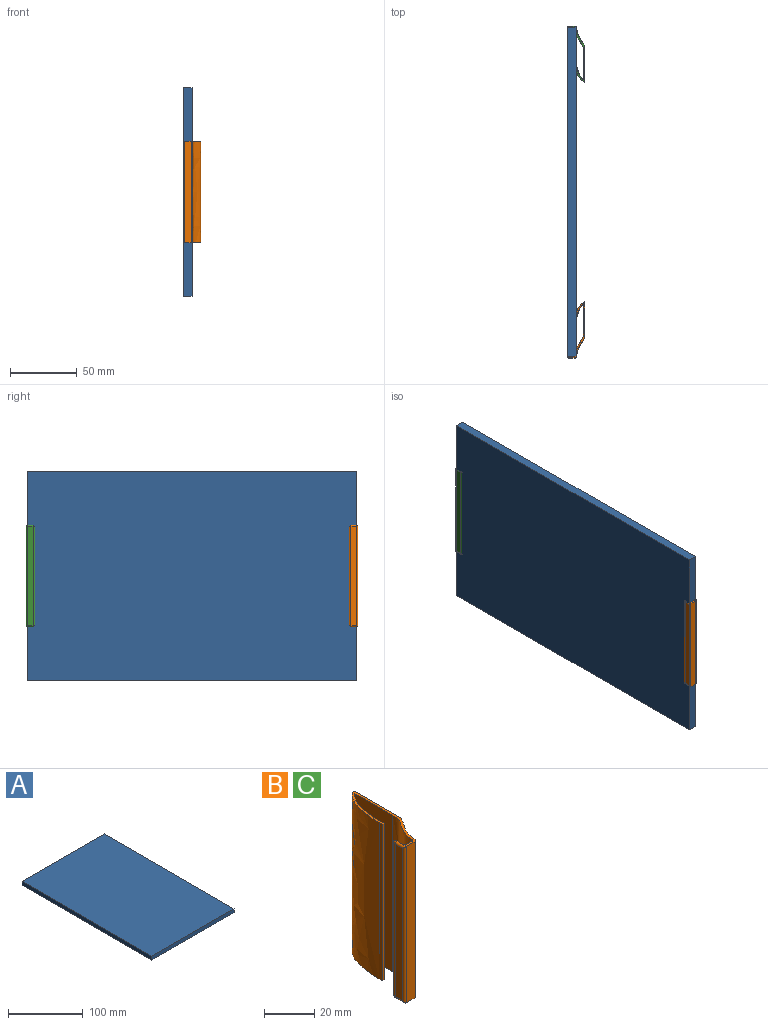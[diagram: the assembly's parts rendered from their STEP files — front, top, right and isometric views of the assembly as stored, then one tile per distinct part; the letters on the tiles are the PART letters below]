
ASSEMBLY  parts=3 mates=2
PART A: 6 faces, bbox 155.6x246.1x6.4 mm
  f0: plane 155.58x6.35mm, normal (0,-1,0), area 987.9mm2, adj f1,f3,f4,f5
  f1: plane 246.06x6.35mm, normal (1,0,0), area 1562.5mm2, adj f0,f2,f4,f5
  f2: plane 155.58x6.35mm, normal (0,1,0), area 987.9mm2, adj f1,f3,f4,f5
  f3: plane 246.06x6.35mm, normal (-1,0,0), area 1562.5mm2, adj f0,f2,f4,f5
  f4: plane 246.06x155.58mm, normal (0,0,1), area 38281.2mm2, adj f0,f1,f2,f3
  f5: plane 246.06x155.58mm, normal (0,0,-1), area 38281.2mm2, adj f0,f1,f2,f3
PART B: 24 faces, bbox 13.5x41.8x76.2 mm
  f0: plane 76.2x1.94mm, normal (-1,0,0), area 147.6mm2, adj f1,f12,f13,f14
  f1: plane 76.2x1mm, normal (0,-1,0), area 76.2mm2, adj f0,f2,f13,f14
  f2: plane 76.2x1.94mm, normal (1,0,0), area 147.6mm2, adj f1,f3,f13,f14
  f3: extruded ~76.2x20.98mm, area 1720.4mm2, adj f2,f4,f13,f14
  f4: plane 76.2x21.33mm, normal (-1,0,0), area 1625.2mm2, adj f3,f5,f13,f14
  f5: extruded ~76.2x17mm, area 1411.4mm2, adj f4,f13,f14,f21
  f6: plane 76.2x3.02mm, normal (0,1,0), area 230.2mm2, adj f13,f14,f21,f22
  f7: plane 76.2x5mm, normal (1,0,0), area 380.5mm2, adj f15,f16,f17,f19,f20,f22
  f8: plane 74.2x4.27mm, normal (-1,0,0), area 316.7mm2, adj f15,f17,f18,f19
  f9: plane 76.2x5.02mm, normal (0,-1,0), area 382.4mm2, adj f13,f14,f18,f23
  f10: extruded ~76.2x15.82mm, area 1323.9mm2, adj f11,f13,f14,f23
  f11: plane 76.2x25mm, normal (1,0,0), area 1905mm2, adj f10,f12,f13,f14
  f12: extruded ~76.2x22.48mm, area 1924.8mm2, adj f0,f11,f13,f14
  f13: plane 41.78x12.36mm, normal (0,0,1), area 75.8mm2, adj f0,f1,f2,f3,f4,f5,f6,f9
  f14: plane 41.78x12.36mm, normal (0,0,-1), area 75.8mm2, adj f0,f1,f2,f3,f4,f5,f6,f9
  f15: cylinder r=2mm len=74.2mm, axis (0,0,-1), area 155.4mm2, adj f7,f8,f16,f20
  f16: torus R=1mm, axis (0,0,1), area 2.3mm2, adj f7,f15,f17
  f17: cylinder r=1mm len=5.27mm, axis (0,1,0), area 7.7mm2, adj f7,f8,f13,f16,f18
  f18: cylinder r=1mm len=76.2mm, axis (0,0,-1), area 118.6mm2, adj f8,f9,f17,f19
  f19: cylinder r=1mm len=5.27mm, axis (0,-1,0), area 7.7mm2, adj f7,f8,f14,f18,f20
  f20: torus R=1mm, axis (0,0,1), area 2.3mm2, adj f7,f15,f19
  f21: cylinder r=1mm len=76.2mm, axis (0,0,-1), area 116.1mm2, adj f5,f6,f13,f14
  f22: cylinder r=1mm len=76.2mm, axis (0,0,1), area 119.7mm2, adj f6,f7,f13,f14
  f23: cylinder r=1mm len=76.2mm, axis (0,0,-1), area 116.8mm2, adj f9,f10,f13,f14
PART C: same geometry as B
PLACE A rot(axis=(0,1,0),90deg) t=(120.69,-5.5,56.32)mm
PLACE B t=(27.35,-129.53,18.22)mm
PLACE C rot(axis=(1,0,0),180deg) t=(27.35,118.53,94.42)mm
MATE fastened A.f2 <-> C.f6  axis (0,1,0) through (23.87,117.53,56.32)mm
MATE fastened B.f6 <-> A.f0  axis (0,-1,0) through (23.87,-128.53,56.32)mm
